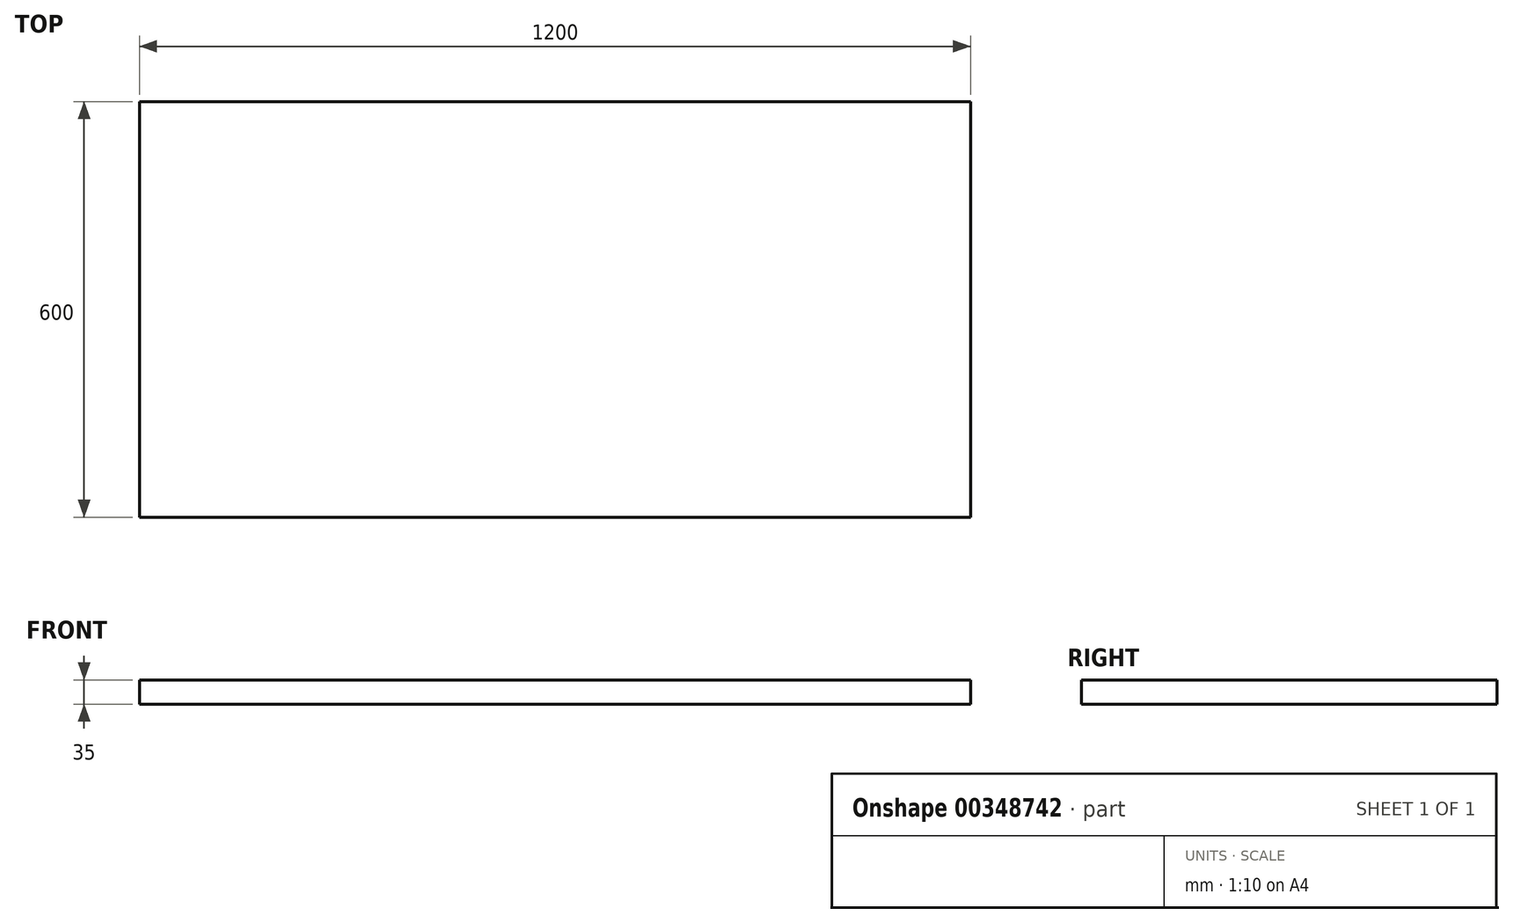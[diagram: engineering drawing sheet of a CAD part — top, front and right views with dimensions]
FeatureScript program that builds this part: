
annotation { "Feature Type Name" : "Feature", "Feature Type Description" : "" }
export const myFeature = defineFeature(function(context is Context, id is Id, definition is map)
    precondition{}
    {
        {
            var Q0;
            Q0=qCreatedBy(makeId("Top.planeOp"),FACE);
            var sketch = newSketch(context, id + "F0", { "sketchPlane" : qUnion([Q0])});
            skLineSegment(sketch, "E0.bottom", {"start": v(-563.32, -301.2) * mm, "end": v(636.68, -301.2) * mm});
            skLineSegment(sketch, "E0.top", {"start": v(-563.32, 298.8) * mm, "end": v(636.68, 298.8) * mm});
            skLineSegment(sketch, "E0.left", {"start": v(-563.32, -301.2) * mm, "end": v(-563.32, 298.8) * mm});
            skLineSegment(sketch, "E0.right", {"start": v(636.68, -301.2) * mm, "end": v(636.68, 298.8) * mm});
            skSolve(sketch);
        }
        {
            var Q0;
            Q0 = qSketchRegion(id + "F0", true);
            extrude(context, id + "F1", {"entities" : qUnion([Q0]), "depth" : 35 * mm});
        }
    });
